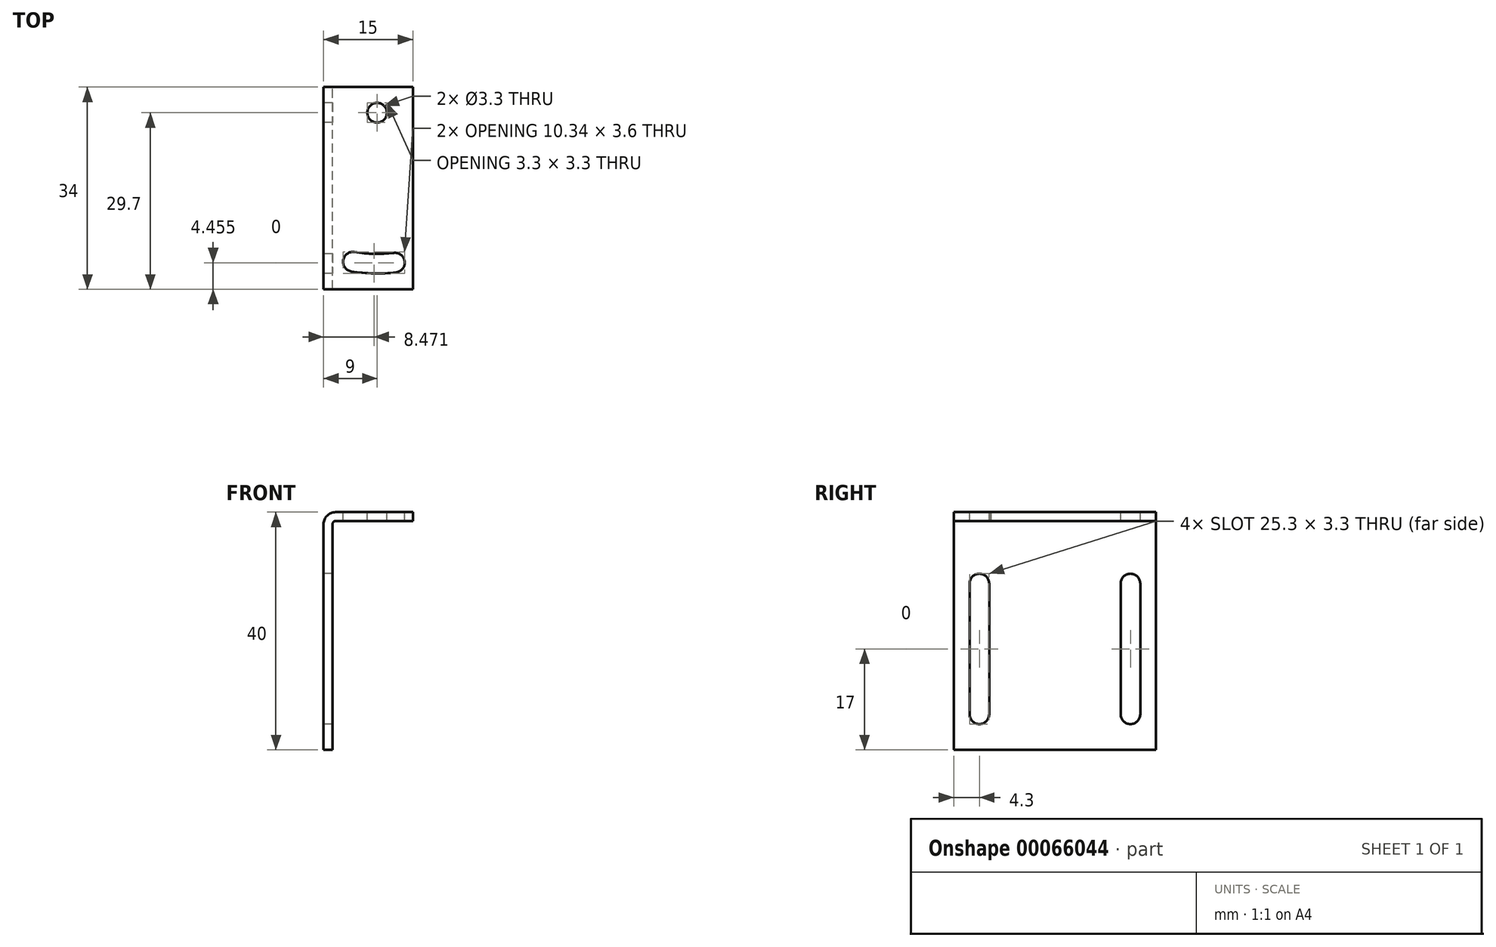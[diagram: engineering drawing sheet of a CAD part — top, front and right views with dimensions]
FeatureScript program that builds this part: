
annotation { "Feature Type Name" : "Feature", "Feature Type Description" : "" }
export const myFeature = defineFeature(function(context is Context, id is Id, definition is map)
    precondition{}
    {
        {
            var Q0;
            Q0=qCreatedBy(makeId("Front.planeOp"),FACE);
            var sketch = newSketch(context, id + "F0", { "sketchPlane" : qUnion([Q0])});
            skLineSegment(sketch, "E0", {"start": v(2, 0) * mm, "end": v(15, 0) * mm});
            skLineSegment(sketch, "E1", {"start": v(15, 0) * mm, "end": v(15, -1.5) * mm});
            skLineSegment(sketch, "E2", {"start": v(15, -1.5) * mm, "end": v(2, -1.5) * mm});
            skLineSegment(sketch, "E3", {"start": v(1.5, -2) * mm, "end": v(1.5, -40) * mm});
            skLineSegment(sketch, "E4", {"start": v(1.5, -40) * mm, "end": v(0, -40) * mm});
            skLineSegment(sketch, "E5", {"start": v(0, -40) * mm, "end": v(0, -2) * mm});
            skPoint(sketch, "E6.visualSharp", {"position": v(1.5, -1.5) * mm});
            skArc(sketch, "E6.filletArc", {"start": v(2, -1.5) * mm, "mid": v(1.65, -1.65) * mm, "end": v(1.5, -2) * mm});
            skPoint(sketch, "E7.visualSharp", {"position": v(0, 0) * mm});
            skArc(sketch, "E7.filletArc", {"start": v(2, 0) * mm, "mid": v(0.59, -0.59) * mm, "end": v(0, -2) * mm});
            skSolve(sketch);
        }
        {
            var Q0;
            Q0 = qSketchRegion(id + "F0", true);
            extrude(context, id + "F1", {"entities" : qUnion([Q0]), "endBound" : BoundingType.SYMMETRIC, "depth" : 34 * mm});
        }
        {
            var Q0;
            Q0=qCreatedBy(makeId("Top.planeOp"),FACE);
            var sketch = newSketch(context, id + "F2", { "sketchPlane" : qUnion([Q0])});
            skPoint(sketch, "E8", {"position": v(9, 12.7) * mm});
            skArc(sketch, "E9", {"start": v(12, -12.52) * mm, "mid": v(8.46, -12.7) * mm, "end": v(4.93, -12.37) * mm});
            skLineSegment(sketch, "E10", {"start": v(12, -12.52) * mm, "end": v(9, 12.7) * mm, "construction": true});
            skLineSegment(sketch, "E11", {"start": v(4.93, -12.37) * mm, "end": v(9, 12.7) * mm, "construction": true});
            skArc(sketch, "E12.0.startCap", {"start": v(11.8, -10.88) * mm, "mid": v(13.64, -12.33) * mm, "end": v(12.2, -14.16) * mm});
            skArc(sketch, "E12.0.endCap", {"start": v(4.67, -14) * mm, "mid": v(3.3, -12.1) * mm, "end": v(5.2, -10.74) * mm});
            skArc(sketch, "E12.0.left", {"start": v(12.2, -14.16) * mm, "mid": v(8.43, -14.34) * mm, "end": v(4.67, -14) * mm});
            skArc(sketch, "E12.0.right", {"start": v(11.8, -10.88) * mm, "mid": v(8.5, -11.04) * mm, "end": v(5.2, -10.74) * mm});
            skCircle(sketch, "E13", {"center": v(9, 12.7) * mm, "radius": 1.65 * mm});
            skSolve(sketch);
        }
        {
            var Q0;
            Q0 = qSketchRegion(id + "F2", true);
            extrude(context, id + "F3", {"entities" : qUnion([Q0]), "operationType" : NewBodyOperationType.REMOVE, "endBound" : BoundingType.THROUGH_ALL, "oppositeDirection" : true, "depth" : 25 * mm});
        }
        {
            var Q0;
            Q0=qCreatedBy(makeId("Right.planeOp"),FACE);
            var sketch = newSketch(context, id + "F4", { "sketchPlane" : qUnion([Q0])});
            skLineSegment(sketch, "E14.rect.bottom", {"start": v(12.7, -34) * mm, "end": v(-12.7, -34) * mm, "construction": true});
            skLineSegment(sketch, "E14.rect.top", {"start": v(12.7, -12) * mm, "end": v(-12.7, -12) * mm, "construction": true});
            skLineSegment(sketch, "E14.rect.left", {"start": v(12.7, -34) * mm, "end": v(12.7, -12) * mm, "construction": true});
            skLineSegment(sketch, "E14.rect.right", {"start": v(-12.7, -34) * mm, "end": v(-12.7, -12) * mm, "construction": true});
            skPoint(sketch, "E14.rect.middle", {"position": v(0, -23) * mm});
            skArc(sketch, "E15.0.startCap", {"start": v(14.35, -34) * mm, "mid": v(12.7, -35.65) * mm, "end": v(11.05, -34) * mm});
            skArc(sketch, "E15.0.endCap", {"start": v(11.05, -12) * mm, "mid": v(12.7, -10.35) * mm, "end": v(14.35, -12) * mm});
            skLineSegment(sketch, "E15.0.left", {"start": v(11.05, -34) * mm, "end": v(11.05, -12) * mm});
            skLineSegment(sketch, "E15.0.right", {"start": v(14.35, -34) * mm, "end": v(14.35, -12) * mm});
            skArc(sketch, "E15.1.startCap", {"start": v(-11.05, -34) * mm, "mid": v(-12.7, -35.65) * mm, "end": v(-14.35, -34) * mm});
            skArc(sketch, "E15.1.endCap", {"start": v(-14.35, -12) * mm, "mid": v(-12.7, -10.35) * mm, "end": v(-11.05, -12) * mm});
            skLineSegment(sketch, "E15.1.left", {"start": v(-14.35, -34) * mm, "end": v(-14.35, -12) * mm});
            skLineSegment(sketch, "E15.1.right", {"start": v(-11.05, -34) * mm, "end": v(-11.05, -12) * mm});
            skSolve(sketch);
        }
        {
            var Q0;
            Q0 = qSketchRegion(id + "F4", true);
            var Q1;
            Q1=sQuery(id+"F4.wireOp",EDGE,"E14.rect.top");
            var Q2;
            Q2=sQuery(id+"F4.wireOp",EDGE,"E14.rect.bottom");
            var Q3;
            Q3=sQuery(id+"F4.wireOp",EDGE,"E14.rect.left");
            var Q4;
            Q4=sQuery(id+"F4.wireOp",EDGE,"E14.rect.right");
            extrude(context, id + "F5", {"entities" : qUnion([Q0]), "operationType" : NewBodyOperationType.REMOVE, "surfaceEntities" : qUnion([Q1, Q2, Q3, Q4]), "endBound" : BoundingType.THROUGH_ALL, "depth" : 10 * mm});
        }
    });
